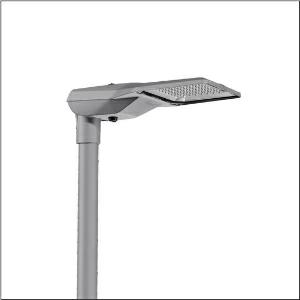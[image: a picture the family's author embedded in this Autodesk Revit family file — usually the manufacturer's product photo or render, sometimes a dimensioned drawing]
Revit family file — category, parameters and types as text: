
# Revit family: streetlight_sl_21_iq_midi___st1_0a_5xe3d21y08mb_afa7
name_source: partatom
category: Lighting Fixtures
units: mm (PartAtom-declared; Revit-internal decimal feet)

## family parameters
Cut with Voids When Loaded = No
Host = Face
Light Source = No
Part Type = Normal
Room Calculation Point = No
Round Connector Dimension = Use Diameter
Shared = No

## types (1)
- --- (1 x LED, 14710 lm, 129.3 W, 2200K)
    Apparent Load = 129 VA
    CIE Flux Codes = 37 72 97 100 100
    Color Rendering = 70
    Color Temperature = 2200K
    Default Elevation = 1800 mm
    Description = Streetlight SL 21 iQ midi, mast luminaire, primary light control with lens, of PMMA, primary optical cover: cover, of toughened safety glass, transparent, light distribution: ST1.0a, light emission: direct distribution, primary light characteristic: asymmetric, installation type: post-top, side-entry, LED, High Power LED, rated luminous flux: 14.710lm, luminous efficacy: 114lm/W, light colour: 722, colour temperature: 2200K, control: pre-setting: logarithmic dimming characteristic, Street-Remote, Auto-Match, Temp-Guard, Lumen-Switch, Night-Set, Smart-Wire, Light-Fading, Desk-Remote (wireless, voltage-free reading and setting of iQ features in the workshop via application-optimized NFC function/RFID function), optimised constant luminous flux control (CLO 2.0), mains connection: 230..240V, AC, 50/60Hz, start of lifetime: 129W, end of service life: 142W, reduction: 56W, luminaire housing, of diecast aluminium, powder-coated, Siteco® metallic grey (DB 702S), corrosivity category C5 mid according to DIN EN ISO 12944, please order mast flange separately, inclination adjustable: 0°, 5°, 10°, 15°, sealing non-destructively replaceable, multi-level sealing system, length: 644mm, width: 335mm, height: 110mm, mast flange for spigot size: 42mm (side-entry): 5XC10008XM4, 60/48mm (side-entry/post-top): 5XC10108XM2, 76/60mm (side-entry/post-top): 5XC10108XM1, Smart Interface below and above, protection rating (complete): IP66, insulation class (complete): insulation class II (safety insulation), certification: CE, ENEC, ENEC+, VDE, impact resistance: IK09, permissible operating ambient temperature for outdoor applications: -40..+50°C, standard-compliant lighting for roads and squares, packaging unit: 1 piece

Light Distribution: ST1.0a
    Height = 111 mm
    Lamp = 1 x LED
    Lamp Light Flux = 14710 lm
    Lamp Power = 129.3 W
    Lamp count = 1
    Length = 644 mm
    Luminous efficacy = 114 lm/W
    Manufacturer = Siteco
    ModVariant = No
    Model = 5XE3D21Y08MB
    Number of Poles = 1
    OnlyDefault = Yes
    Power Factor = 1
    Product Name = Streetlight SL 21 iQ midi | ST1.0a
    Product group = mast luminaire | pylon top
    ProductGroupID = 6100
    Protection Class = Protection class II
    Protection Degree = IP 66
    RLX_Detail_Level = 1
    RLX_Emergency_Light_Flux = 0 lm
    RLX_Emergency_Type = 0
    RLX_Emergency_Type_DB = No
    RlxData = <blob elided: 91377 chars, md5=00f0af66>
    Socket = socket
    Standby Power = 0 W
    System Light Flux = 14710 lm
    System Power = 129 W
    Type Comments = factory setting: luminous flux: 100 % | dim-lin: 254 | 672 mA
    Type Image = l_1004304.jpg
    URL = http://relux.com
    VarID = @adj_083453
    Voltage = 0 V
    Weight = 0.00 kg
    Width = 336 mm

## geometry (parser evidence)
native form markers: Blend x4, Sweep x12
no freeform markers — native parametric forms only
